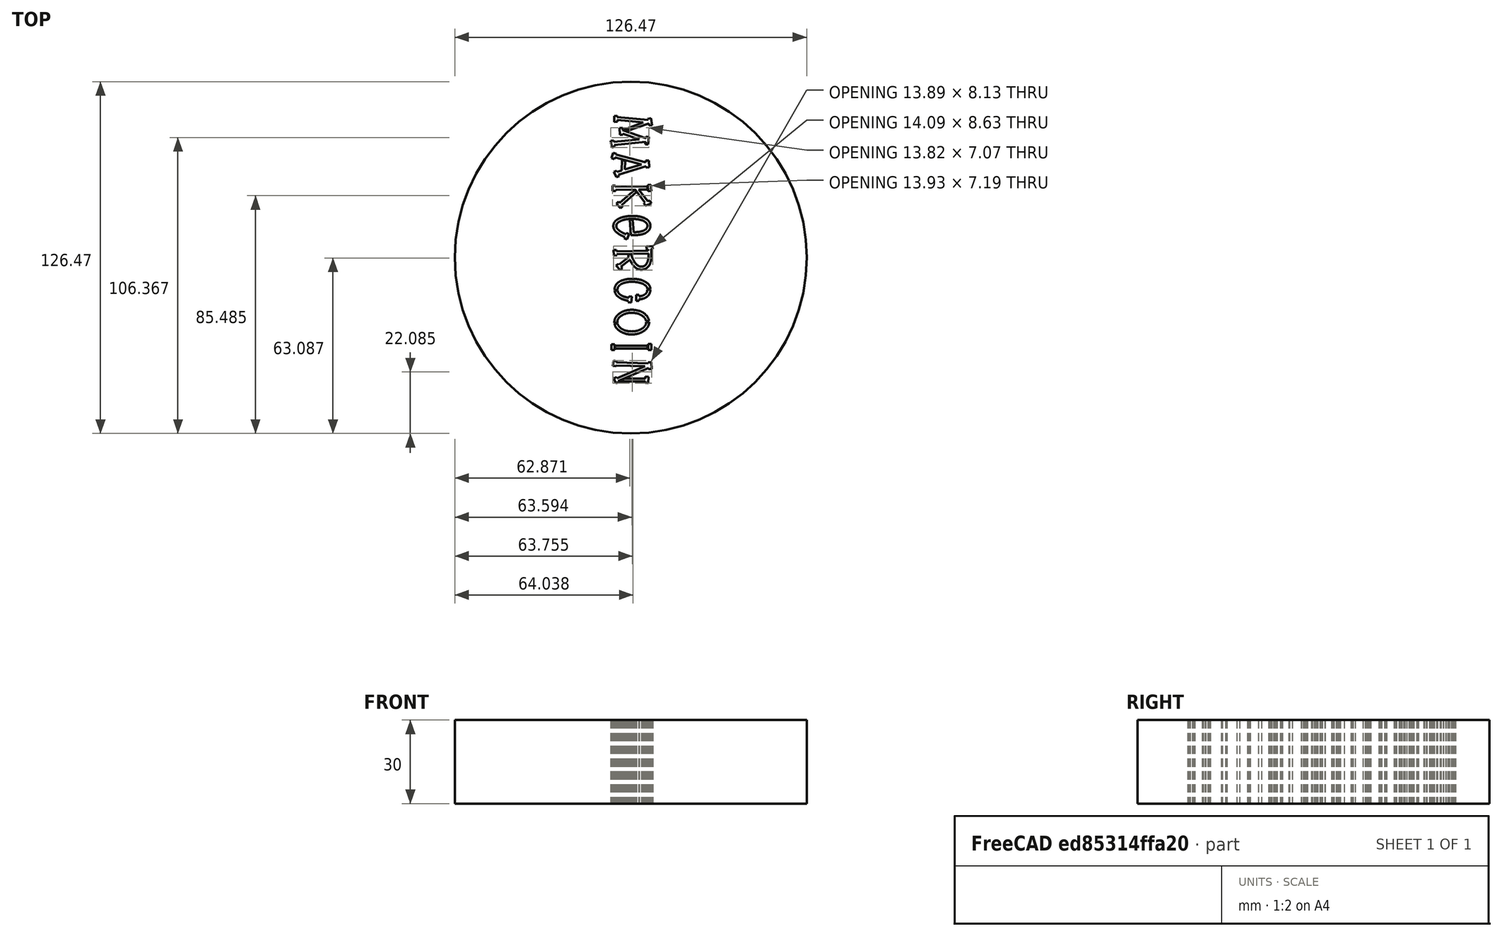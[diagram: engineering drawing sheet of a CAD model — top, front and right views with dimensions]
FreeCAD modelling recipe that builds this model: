
FCSTD DOCUMENT  (FreeCAD 0.21R33771 (Git))
Label: tekstDavlennij
License: All rights reserved
LicenseURL: http://en.wikipedia.org/wiki/All_rights_reserved
objects: Part::Part2DObjectPython×1, Sketcher::SketchObject×1, PartDesign::Pad×1, PartDesign::Pocket×1, PartDesign::Body×1
note: 7 computed .brp shape members not serialized (recipe doc carries the construction recipe); baked Part::Feature solids carry a one-line shape summary decoded from their .brp

FEATURE [Part::Part2DObjectPython] ShapeString001  # Draft 2D object (typed FeaturePython)
  FontFile = <userpath>/Downloads/brownie-stencil-font/BrownieStencil-8O8MJ.ttf
  MakeFace = false
  Placement = pos=(-3.56,34.08,10.87) rot=(0,0,-1;1.5708rad)
  Size = 7
  String = MakerCoin
  Tracking = 3
FEATURE [Sketcher::SketchObject] Sketch002
  FullyConstrained = false
  MapMode = 5
  Support = -> [XY_Plane001]
  sketch-geometry (1):
    g0: Circle CenterX=2.22384 CenterY=-16.9649 CenterZ=0 NormalX=0 NormalY=0 NormalZ=1 AngleXU=0 Radius=63.2388
FEATURE [PartDesign::Pad] Pad
  Direction = (0,0,1)
  Length = 30
  Length2 = 10
  Profile = -> Sketch002
  ReferenceAxis = -> Sketch002 [N_Axis]
  Refine = true
  Type = 0
FEATURE [PartDesign::Pocket] Pocket001
  BaseFeature = -> Pad
  Direction = (0,0,-1)
  Length = 5
  Length2 = 5
  Midplane = true
  Profile = -> ShapeString001
  ReferenceAxis = -> ShapeString001 [N_Axis]
  Refine = true
  Type = 1
FEATURE [PartDesign::Body] Body001
  Group = -> [ShapeString001,Sketch002,Pad,Pocket001]
  Origin = -> Origin001
  Tip = -> Pocket001
